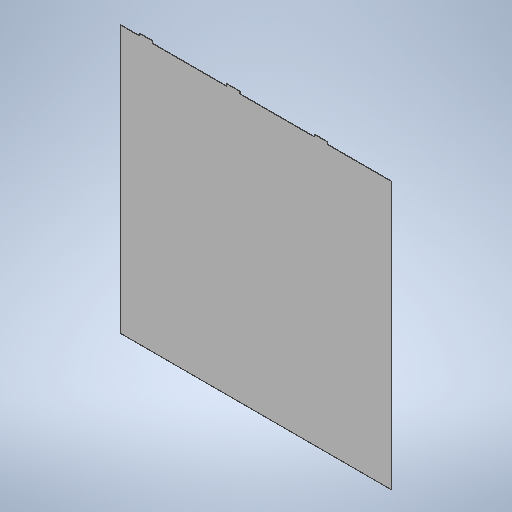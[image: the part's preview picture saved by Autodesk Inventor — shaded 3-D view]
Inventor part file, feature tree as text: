
AUTODESK INVENTOR PART (.ipt)
format: ipt  version: 2025.1 (Build 291241020, 241B)  size: 272,896 bytes
history: native  units: in
note: dims shown in document units (in); Inventor stores cm internally (conversion verified against a paired STEP export)
features: extrude x1, sketch x1
ambient origin geometry x8: Origin, YZ Plane, XZ Plane, XY Plane, X Axis, Y Axis, Z Axis, Center Point
bodies: Solid1 (feature_tree)
feature tree (2):
  extrude  "Extrusion1"  Depth=6.2in
  sketch  "Sketch1"  dims[d0=6.1in d1=6.2in d4=0.3in d8=0.3in d10=4.434in d11=0.05in d12=0.434in d13=0.05in d14=0.3in d15=0.3in d16=0.05in d17=0.01in d18=0.0in]
